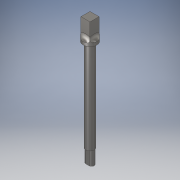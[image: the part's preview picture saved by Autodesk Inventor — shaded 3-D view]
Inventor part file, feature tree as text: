
AUTODESK INVENTOR PART (.ipt)
format: ipt  version: 2019 (Build 230136000, 136)  size: 217,600 bytes
history: native  units: mm
features: extrude x4, sketch x4, other x1, fillet x1
ambient origin geometry x8: Origin, YZ Plane, XZ Plane, XY Plane, X Axis, Y Axis, Z Axis, Center Point
bodies: Body1 (feature_tree)
feature tree (10):
  other  "Sólido1"
  extrude  "Extrusión1"  Depth=61.0mm TaperAngle=0.0deg
  extrude  "Extrusión2"  Depth=9.0mm TaperAngle=0.0deg
  extrude  "Extrusión3"  Depth=6.0mm
  fillet  "Empalme1"  Radius=12.0mm
  extrude  "Extrusión4"  Depth=9.0mm
  sketch  "Boceto1"  dims[d0=5.5mm d1=61.0mm d2=0.0mm]
  sketch  "Boceto2"  dims[d3=9.0mm d4=2.0mm d5=0.0mm]
  sketch  "Boceto3"  dims[d6=6.0mm d7=6.0mm d8=12.0mm d9=0.0mm]
  sketch  "Boceto4"  dims[d10=5.5mm d14=5.5mm d15=1.69mm d16=9.0mm d17=0.0mm]
